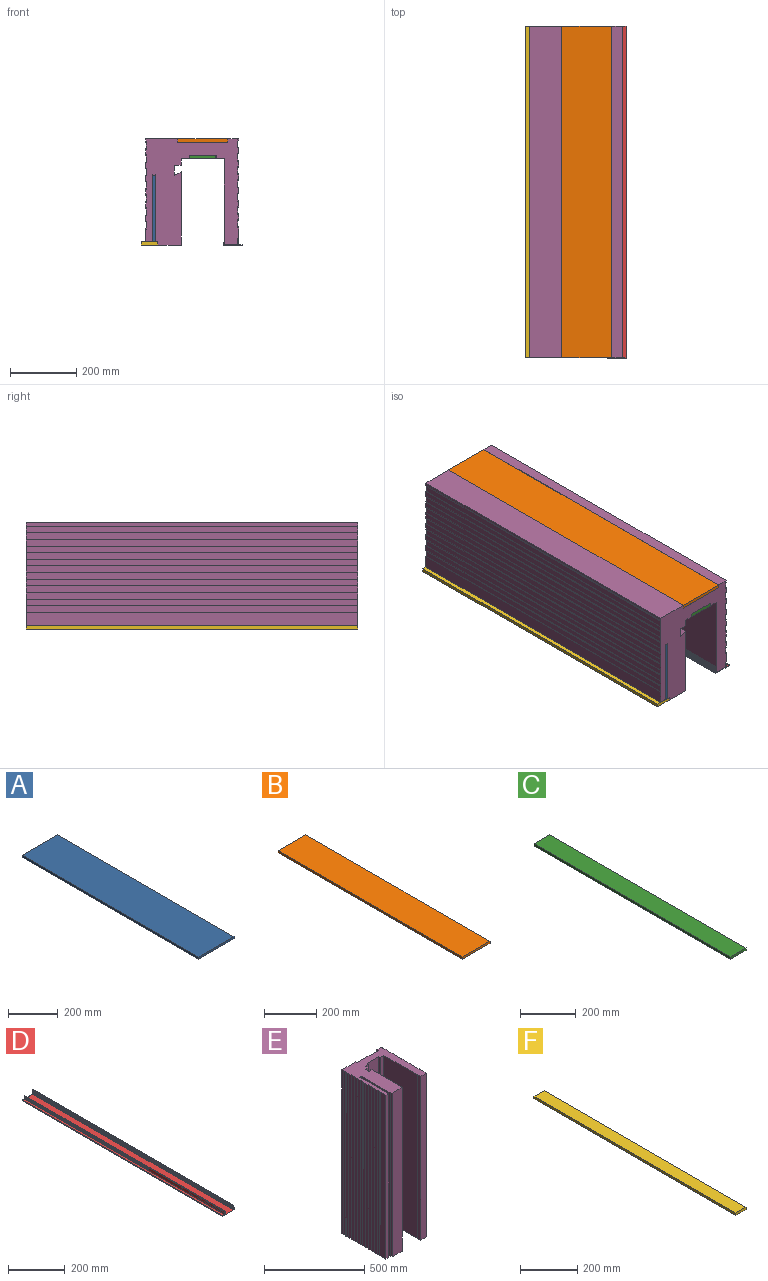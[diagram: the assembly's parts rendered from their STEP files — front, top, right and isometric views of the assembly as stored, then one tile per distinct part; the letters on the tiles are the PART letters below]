
ASSEMBLY  parts=6 mates=5
PART A: 6 faces, bbox 200x1000x10 mm
  f0: plane 1000x10mm, normal (-1,0,0), area 10000mm2, adj f1,f3,f4,f5
  f1: plane 1000x200mm, normal (0,0,-1), area 200000mm2, adj f0,f2,f4,f5
  f2: plane 1000x10mm, normal (1,0,0), area 10000mm2, adj f1,f3,f4,f5
  f3: plane 1000x200mm, normal (0,0,1), area 200000mm2, adj f0,f2,f4,f5
  f4: plane 200x10mm, normal (0,-1,0), area 2000mm2, adj f0,f1,f2,f3
  f5: plane 200x10mm, normal (0,1,0), area 2000mm2, adj f0,f1,f2,f3
PART B: 6 faces, bbox 150x1000x10 mm
  f0: plane 1000x10mm, normal (-1,0,0), area 10000mm2, adj f1,f3,f4,f5
  f1: plane 1000x150mm, normal (0,0,-1), area 150000mm2, adj f0,f2,f4,f5
  f2: plane 1000x10mm, normal (1,0,0), area 10000mm2, adj f1,f3,f4,f5
  f3: plane 1000x150mm, normal (0,0,1), area 150000mm2, adj f0,f2,f4,f5
  f4: plane 150x10mm, normal (0,-1,0), area 1500mm2, adj f0,f1,f2,f3
  f5: plane 150x10mm, normal (0,1,0), area 1500mm2, adj f0,f1,f2,f3
PART C: 6 faces, bbox 80x1000x10 mm
  f0: plane 1000x10mm, normal (-1,0,0), area 10000mm2, adj f1,f3,f4,f5
  f1: plane 1000x80mm, normal (0,0,-1), area 80000mm2, adj f0,f2,f4,f5
  f2: plane 1000x10mm, normal (1,0,0), area 10000mm2, adj f1,f3,f4,f5
  f3: plane 1000x80mm, normal (0,0,1), area 80000mm2, adj f0,f2,f4,f5
  f4: plane 80x10mm, normal (0,-1,0), area 800mm2, adj f0,f1,f2,f3
  f5: plane 80x10mm, normal (0,1,0), area 800mm2, adj f0,f1,f2,f3
PART D: 62 faces, bbox 57.5x1000x21 mm
  f0: plane 1000x14.3mm, normal (-1,0,0), area 14303.9mm2, adj f1,f2,f60,f61
  f1: plane 57.5x21mm, normal (0,-1,0), area 145.8mm2, adj f0,f2,f3,f4,f5,f6,f7,f8
  f2: plane 1000x11mm, normal (0,0,1), area 11000mm2, adj f0,f1,f3,f60
  f3: plane 1000x1.5mm, normal (1,0,0), area 1500mm2, adj f1,f2,f4,f60
  f4: plane 1000x1.5mm, normal (0,0,1), area 1500mm2, adj f1,f3,f5,f60
  f5: plane 1000x3mm, normal (-1,0,0), area 3000mm2, adj f1,f4,f6,f60
  f6: plane 1000x57.5mm, normal (0,0,-1), area 57500mm2, adj f1,f5,f7,f60
  f7: plane 1000x4mm, normal (1,0,0), area 4000mm2, adj f1,f6,f8,f60
  f8: plane 1000x1mm, normal (0,0,1), area 1000mm2, adj f1,f7,f9,f60
  f9: plane 1000x3mm, normal (-1,0,0), area 3000mm2, adj f1,f8,f10,f60
  f10: plane 1000x1mm, normal (0,0,1), area 1000mm2, adj f1,f9,f11,f60
  f11: plane 1000x7mm, normal (1,0,0), area 7000mm2, adj f1,f10,f12,f60
  f12: plane 1000x1mm, normal (0,0,-1), area 1000mm2, adj f1,f11,f13,f60
  f13: plane 1000x3mm, normal (-1,0,0), area 3000mm2, adj f1,f12,f14,f60
  f14: plane 1000x1mm, normal (0,0,-1), area 1000mm2, adj f1,f13,f15,f60
  f15: plane 1000x4mm, normal (1,0,0), area 4000mm2, adj f1,f14,f16,f60
  f16: plane 1000x2mm, normal (0,0,1), area 2000mm2, adj f1,f15,f17,f60
  f17: plane 1000x12mm, normal (1,0,0), area 12000mm2, adj f1,f16,f18,f60
  f18: plane 1000x1mm, normal (0,0,1), area 1000mm2, adj f1,f17,f19,f60
  f19: plane 1000x1.73mm, normal (-0.87,0,0.5), area 2000mm2, adj f1,f18,f20,f60
  f20: plane 1000x1mm, normal (0,0,-1), area 1000mm2, adj f1,f19,f21,f60
  f21: plane 1000x1.73mm, normal (-0.87,0,0.5), area 2000mm2, adj f1,f20,f22,f60
  f22: plane 1000x1mm, normal (0,0,-1), area 1000mm2, adj f1,f21,f23,f60
  f23: plane 1000x1.73mm, normal (-0.87,0,0.5), area 2000mm2, adj f1,f22,f24,f60
  f24: plane 1000x1mm, normal (0,0,-1), area 1000mm2, adj f1,f23,f25,f60
  f25: plane 1000x1.73mm, normal (-0.87,0,0.5), area 2000mm2, adj f1,f24,f26,f60
  f26: plane 1000x1mm, normal (0,0,-1), area 1000mm2, adj f1,f25,f27,f60
  f27: plane 1000x1.73mm, normal (-0.87,0,0.5), area 2000mm2, adj f1,f26,f28,f60
  f28: plane 1000x1mm, normal (0,0,-1), area 1000mm2, adj f1,f27,f29,f60
  f29: plane 1000x1.73mm, normal (-0.87,0,0.5), area 2000mm2, adj f1,f28,f30,f60
  f30: plane 1000x1mm, normal (0,0,-1), area 1000mm2, adj f1,f29,f31,f60
  f31: plane 1000x1.73mm, normal (-0.87,0,0.5), area 2000mm2, adj f1,f30,f32,f60
  f32: plane 1000x1mm, normal (0,0,-1), area 1000mm2, adj f1,f31,f33,f60
  f33: plane 1000x1.73mm, normal (-0.87,0,0.5), area 2000mm2, adj f1,f32,f34,f60
  f34: plane 1000x1mm, normal (0,0,-1), area 1000mm2, adj f1,f33,f35,f60
  f35: plane 1000x1.73mm, normal (-0.87,0,0.5), area 2000mm2, adj f1,f34,f36,f60
  f36: plane 1000x1mm, normal (0,0,-1), area 1000mm2, adj f1,f35,f37,f60
  f37: plane 1000x1.73mm, normal (-0.87,0,0.5), area 2000mm2, adj f1,f36,f38,f60
  f38: plane 1000x1mm, normal (0,0,-1), area 1000mm2, adj f1,f37,f39,f60
  f39: plane 1000x1.73mm, normal (-0.87,0,0.5), area 2000mm2, adj f1,f38,f40,f60
  f40: plane 1000x1mm, normal (0,0,-1), area 1000mm2, adj f1,f39,f41,f60
  f41: plane 1000x0.45mm, normal (-1,0,0), area 447.4mm2, adj f1,f40,f42,f60
  f42: plane 1000x41mm, normal (0,0,1), area 41000mm2, adj f1,f41,f43,f60
  f43: plane 1000x0.45mm, normal (1,0,0), area 447.4mm2, adj f1,f42,f44,f60
  f44: plane 1000x1mm, normal (0,0,-1), area 1000mm2, adj f1,f43,f45,f60
  f45: plane 1000x1.73mm, normal (0.87,0,0.5), area 2000mm2, adj f1,f44,f46,f60
  f46: plane 1000x1mm, normal (0,0,-1), area 1000mm2, adj f1,f45,f47,f60
  f47: plane 1000x1.73mm, normal (0.87,0,0.5), area 2000mm2, adj f1,f46,f48,f60
  f48: plane 1000x1mm, normal (0,0,-1), area 1000mm2, adj f1,f47,f49,f60
  f49: plane 1000x1.73mm, normal (0.87,0,0.5), area 2000mm2, adj f1,f48,f50,f60
  f50: plane 1000x1mm, normal (0,0,-1), area 1000mm2, adj f1,f49,f51,f60
  f51: plane 1000x1.73mm, normal (0.87,0,0.5), area 2000mm2, adj f1,f50,f52,f60
  f52: plane 1000x1mm, normal (0,0,-1), area 1000mm2, adj f1,f51,f53,f60
  f53: plane 1000x1.73mm, normal (0.87,0,0.5), area 2000mm2, adj f1,f52,f54,f60
  f54: plane 1000x1mm, normal (0,0,-1), area 1000mm2, adj f1,f53,f55,f60
  f55: plane 1000x1.73mm, normal (0.87,0,0.5), area 2000mm2, adj f1,f54,f56,f60
  f56: plane 1000x1mm, normal (0,0,-1), area 1000mm2, adj f1,f55,f57,f60
  f57: plane 1000x1.73mm, normal (0.87,0,0.5), area 2000mm2, adj f1,f56,f58,f60
  f58: plane 1000x1mm, normal (0,0,-1), area 1000mm2, adj f1,f57,f59,f60
  f59: plane 1000x1.73mm, normal (0.87,0,0.5), area 2000mm2, adj f1,f58,f60,f61
  f60: plane 57.5x21mm, normal (0,1,0), area 145.8mm2, adj f0,f2,f3,f4,f5,f6,f7,f8
  f61: plane 1000x1mm, normal (0,0,1), area 1000mm2, adj f0,f1,f59,f60
PART E: 88 faces, bbox 280x320x1000 mm
  f0: plane 1000x20mm, normal (-1,0,0), area 20000mm2, adj f44,f45,f82,f86
  f1: plane 1000x20mm, normal (-1,0,0), area 20000mm2, adj f44,f45,f79,f83
  f2: plane 1000x20mm, normal (-1,0,0), area 20000mm2, adj f44,f45,f76,f80
  f3: plane 1000x20mm, normal (-1,0,0), area 20000mm2, adj f44,f45,f73,f77
  f4: plane 1000x20mm, normal (-1,0,0), area 20000mm2, adj f44,f45,f70,f74
  f5: plane 1000x20mm, normal (-1,0,0), area 20000mm2, adj f44,f45,f67,f71
  f6: plane 1000x10mm, normal (-1,0,0), area 10000mm2, adj f15,f44,f45,f68
  f7: plane 1000x35mm, normal (1,0,0), area 35000mm2, adj f39,f44,f45,f64
  f8: plane 1000x20mm, normal (1,0,0), area 20000mm2, adj f44,f45,f61,f65
  f9: plane 1000x20mm, normal (1,0,0), area 20000mm2, adj f44,f45,f58,f62
  f10: plane 1000x20mm, normal (1,0,0), area 20000mm2, adj f44,f45,f55,f59
  f11: plane 1000x20mm, normal (1,0,0), area 20000mm2, adj f44,f45,f52,f56
  f12: plane 1000x20mm, normal (1,0,0), area 20000mm2, adj f44,f45,f49,f53
  f13: plane 1000x20mm, normal (1,0,0), area 20000mm2, adj f44,f45,f46,f50
  f14: plane 1000x10mm, normal (1,0,0), area 10000mm2, adj f15,f43,f44,f45
  f15: plane 1000x96.75mm, normal (0,1,0), area 96750mm2, adj f6,f14,f44,f45
  f16: plane 1000x40mm, normal (-1,0,0), area 40000mm2, adj f17,f44,f45,f85
  f17: plane 1000x20.5mm, normal (0,-1,0), area 20500mm2, adj f16,f18,f44,f45
  f18: plane 1000x202mm, normal (1,0,0), area 202000mm2, adj f17,f19,f44,f45
  f19: cylinder r=10mm len=1000mm, axis (0,0,-1), area 11054.3mm2, adj f18,f20,f44,f45
  f20: plane 1000x202mm, normal (-1,0,0), area 202000mm2, adj f19,f21,f44,f45
  f21: plane 1000x6mm, normal (0,-1,0), area 6000mm2, adj f20,f22,f44,f45
  f22: plane 1000x10mm, normal (-1,0,0), area 10000mm2, adj f21,f23,f44,f45
  f23: plane 1000x70mm, normal (0,-1,0), area 70000mm2, adj f22,f24,f44,f45
  f24: plane 1000x220.19mm, normal (1,0,0), area 220190.5mm2, adj f23,f25,f44,f45
  f25: plane 1000x20mm, normal (-0.45,0.89,0), area 22446.5mm2, adj f24,f26,f44,f45
  f26: plane 1000x30mm, normal (1,0,0), area 30000mm2, adj f25,f27,f44,f45
  f27: plane 1000x20mm, normal (0,-1,0), area 20000mm2, adj f26,f28,f44,f45
  f28: plane 1000x20mm, normal (1,0,0), area 20000mm2, adj f27,f29,f44,f45
  f29: plane 1000x24.75mm, normal (0,-1,0), area 24750mm2, adj f28,f30,f44,f45
  f30: plane 1000x10mm, normal (1,0,0), area 10000mm2, adj f29,f31,f44,f45
  f31: plane 1000x80.5mm, normal (0,-1,0), area 80500mm2, adj f30,f32,f44,f45
  f32: plane 1000x10mm, normal (-1,0,0), area 10000mm2, adj f31,f33,f44,f45
  f33: plane 1000x24.75mm, normal (0,-1,0), area 24750mm2, adj f32,f34,f44,f45
  f34: plane 1000x237.5mm, normal (-1,0,0), area 237500mm2, adj f33,f35,f44,f45
  f35: plane 1000x2mm, normal (0,-1,0), area 2000mm2, adj f34,f36,f44,f45
  f36: plane 1000x21.5mm, normal (-1,0,0), area 21500mm2, adj f35,f37,f44,f45
  f37: plane 1000x39.1mm, normal (0,-1,0), area 39100mm2, adj f36,f38,f44,f45
  f38: plane 1000x18.5mm, normal (1,0,0), area 18500mm2, adj f37,f39,f44,f45
  f39: plane 1000x1.9mm, normal (0,-1,0), area 1900mm2, adj f7,f38,f44,f45
  f40: plane 1000x5.5mm, normal (1,0,0), area 5500mm2, adj f41,f44,f45,f47
  f41: plane 1000x32.75mm, normal (0,1,0), area 32750mm2, adj f40,f42,f44,f45
  f42: plane 1000x10mm, normal (-1,0,0), area 10000mm2, adj f41,f43,f44,f45
  f43: plane 1000x150.5mm, normal (0,1,0), area 150500mm2, adj f14,f42,f44,f45
  f44: plane 320x280mm, normal (0,0,1), area 49774.3mm2, adj f0,f1,f2,f3,f4,f5,f6,f7
  f45: plane 320x280mm, normal (0,0,-1), area 49774.3mm2, adj f0,f1,f2,f3,f4,f5,f6,f7
  f46: plane 1000x2mm, normal (-0.71,0.71,0), area 2828.4mm2, adj f13,f44,f45,f48
  f47: plane 1000x2mm, normal (-0.71,-0.71,0), area 2828.4mm2, adj f40,f44,f45,f48
  f48: plane 1000x24mm, normal (1,0,0), area 24000mm2, adj f44,f45,f46,f47
  f49: plane 1000x2mm, normal (-0.71,0.71,0), area 2828.4mm2, adj f12,f44,f45,f51
  f50: plane 1000x2mm, normal (-0.71,-0.71,0), area 2828.4mm2, adj f13,f44,f45,f51
  f51: plane 1000x24mm, normal (1,0,0), area 24000mm2, adj f44,f45,f49,f50
  f52: plane 1000x2mm, normal (-0.71,0.71,0), area 2828.4mm2, adj f11,f44,f45,f54
  f53: plane 1000x2mm, normal (-0.71,-0.71,0), area 2828.4mm2, adj f12,f44,f45,f54
  f54: plane 1000x24mm, normal (1,0,0), area 24000mm2, adj f44,f45,f52,f53
  f55: plane 1000x2mm, normal (-0.71,0.71,0), area 2828.4mm2, adj f10,f44,f45,f57
  f56: plane 1000x2mm, normal (-0.71,-0.71,0), area 2828.4mm2, adj f11,f44,f45,f57
  f57: plane 1000x24mm, normal (1,0,0), area 24000mm2, adj f44,f45,f55,f56
  f58: plane 1000x2mm, normal (-0.71,0.71,0), area 2828.4mm2, adj f9,f44,f45,f60
  f59: plane 1000x2mm, normal (-0.71,-0.71,0), area 2828.4mm2, adj f10,f44,f45,f60
  f60: plane 1000x24mm, normal (1,0,0), area 24000mm2, adj f44,f45,f58,f59
  f61: plane 1000x2mm, normal (-0.71,0.71,0), area 2828.4mm2, adj f8,f44,f45,f63
  f62: plane 1000x2mm, normal (-0.71,-0.71,0), area 2828.4mm2, adj f9,f44,f45,f63
  f63: plane 1000x24mm, normal (1,0,0), area 24000mm2, adj f44,f45,f61,f62
  f64: plane 1000x2mm, normal (-0.71,0.71,0), area 2828.4mm2, adj f7,f44,f45,f66
  f65: plane 1000x2mm, normal (-0.71,-0.71,0), area 2828.4mm2, adj f8,f44,f45,f66
  f66: plane 1000x24mm, normal (1,0,0), area 24000mm2, adj f44,f45,f64,f65
  f67: plane 1000x2mm, normal (0.71,0.71,0), area 2828.4mm2, adj f5,f44,f45,f69
  f68: plane 1000x2mm, normal (0.71,-0.71,0), area 2828.4mm2, adj f6,f44,f45,f69
  f69: plane 1000x24mm, normal (-1,0,0), area 24000mm2, adj f44,f45,f67,f68
  f70: plane 1000x2mm, normal (0.71,0.71,0), area 2828.4mm2, adj f4,f44,f45,f72
  f71: plane 1000x2mm, normal (0.71,-0.71,0), area 2828.4mm2, adj f5,f44,f45,f72
  f72: plane 1000x24mm, normal (-1,0,0), area 24000mm2, adj f44,f45,f70,f71
  f73: plane 1000x2mm, normal (0.71,0.71,0), area 2828.4mm2, adj f3,f44,f45,f75
  f74: plane 1000x2mm, normal (0.71,-0.71,0), area 2828.4mm2, adj f4,f44,f45,f75
  f75: plane 1000x24mm, normal (-1,0,0), area 24000mm2, adj f44,f45,f73,f74
  f76: plane 1000x2mm, normal (0.71,0.71,0), area 2828.4mm2, adj f2,f44,f45,f78
  f77: plane 1000x2mm, normal (0.71,-0.71,0), area 2828.4mm2, adj f3,f44,f45,f78
  f78: plane 1000x24mm, normal (-1,0,0), area 24000mm2, adj f44,f45,f76,f77
  f79: plane 1000x2mm, normal (0.71,0.71,0), area 2828.4mm2, adj f1,f44,f45,f81
  f80: plane 1000x2mm, normal (0.71,-0.71,0), area 2828.4mm2, adj f2,f44,f45,f81
  f81: plane 1000x24mm, normal (-1,0,0), area 24000mm2, adj f44,f45,f79,f80
  f82: plane 1000x2mm, normal (0.71,0.71,0), area 2828.4mm2, adj f0,f44,f45,f84
  f83: plane 1000x2mm, normal (0.71,-0.71,0), area 2828.4mm2, adj f1,f44,f45,f84
  f84: plane 1000x24mm, normal (-1,0,0), area 24000mm2, adj f44,f45,f82,f83
  f85: plane 1000x2mm, normal (0.71,0.71,0), area 2828.4mm2, adj f16,f44,f45,f87
  f86: plane 1000x2mm, normal (0.71,-0.71,0), area 2828.4mm2, adj f0,f44,f45,f87
  f87: plane 1000x24mm, normal (-1,0,0), area 24000mm2, adj f44,f45,f85,f86
PART F: 6 faces, bbox 50x1000x10 mm
  f0: plane 1000x10mm, normal (-1,0,0), area 10000mm2, adj f1,f3,f4,f5
  f1: plane 1000x50mm, normal (0,0,-1), area 50000mm2, adj f0,f2,f4,f5
  f2: plane 1000x10mm, normal (1,0,0), area 10000mm2, adj f1,f3,f4,f5
  f3: plane 1000x50mm, normal (0,0,1), area 50000mm2, adj f0,f2,f4,f5
  f4: plane 50x10mm, normal (0,-1,0), area 500mm2, adj f0,f1,f2,f3
  f5: plane 50x10mm, normal (0,1,0), area 500mm2, adj f0,f1,f2,f3
PLACE A rot(axis=(0,1,0),90deg) t=(-266.83,500,-44.72)mm
PLACE B t=(-190.83,500,55.28)mm fixed
PLACE C t=(-155.83,500,5.28)mm
PLACE D rot(axis=(0,0,1),180deg) t=(-52.58,-500,-255.22)mm
PLACE E rot(axis=(1,0,0),90deg) t=(-168.93,500,-120.99)mm
PLACE F t=(-300.58,500,-254.72)mm
MATE fastened A.f4 <-> E.f44  axis (0,-1,0) through (-256.58,-500,-42.72)mm
MATE fastened E.f44 <-> B.f4  axis (0,-1,0) through (-190.83,-500,65.28)mm
MATE fastened C.f4 <-> E.f44  axis (0,-1,0) through (-155.83,-500,15.28)mm
MATE fastened D.f60 <-> E.f44  axis (0,-1,0) through (-48.58,-500,-253.72)mm
MATE fastened F.f4 <-> E.f44  axis (0,-1,0) through (-250.58,-500,-244.72)mm
